# Revit family: BVR-R
name_source: partatom
category: Арматура трубопроводов
units: mm (PartAtom-declared; Revit-internal decimal feet)

## family parameters
Всегда вертикально = Да
На основе рабочей плоскости = Нет
Общий = Нет
При загрузке вырезать с полостями = Нет
Размер круглого соединителя = Использовать диаметр
Тип детали = Вставляется

## types (9) — shared parameters
ADSK_Версия Revit = 2019
ADSK_Версия семейства = 1.0
ADSK_Единица измерения = шт.
ADSK_Завод-изготовитель = ООО «Ридан-Трейд»
ADSK_Количество = 1
ADSK_Материал = Латунь Никелированная
ADSK_Потеря давления жидкости = 0.0 Па
ADSK_Расход жидкости = 0.0000 м³/ч
LT = BVR-R
URL = https://ridan.ru

## per-type parameters (varying)
| type | ADSK_Диаметр условный | ADSK_Код изделия | ADSK_Марка | ADSK_Масса | ADSK_Наименование | ADSK_Пропускная способность | a | b | c | d | e | f | g | h | i | j | k | l | m | n | o | p | УГО_Длина |
| DN15 | 15 мм | 065B8307RG | BVR-R DN15 | 0.23 | Кран шаровой ГОСТ BVR-R полнопроходной с внутренней резьбой PN40, Tmax=120C, DN15 | 15.0000 м³/ч | 18 мм | 4 мм | 2 мм | 10 мм | 1 мм | 11 мм | 15 мм | 7 мм | 29 мм | 24 мм | 31 мм | 25 мм | 19 мм | 16 мм | 29 мм | 29 мм | 29 мм |
| DN20 | 20 мм | 065B8308RG | BVR-R DN20 | 0.33 | Кран шаровой ГОСТ BVR-R полнопроходной с внутренней резьбой PN40, Tmax=120C, DN20 | 28.0000 м³/ч | 19 мм | 4 мм | 3 мм | 15 мм | 2 мм | 11 мм | 18 мм | 9 мм | 36 мм | 31 мм | 38 мм | 31 мм | 24 мм | 16 мм | 33 мм | 33 мм | 33 мм |
| DN25 | 25 мм | 065B8309RG | BVR-R DN25 | 0.55 | Кран шаровой ГОСТ BVR-R полнопроходной с внутренней резьбой PN40, Tmax=120C, DN25 | 39.0000 м³/ч | 23 мм | 5 мм | 3 мм | 17 мм | 1 мм | 12 мм | 22 мм | 11 мм | 45 мм | 38 мм | 47 мм | 38 мм | 30 мм | 19 мм | 40 мм | 39 мм | 39 мм |
| DN32 | 32 мм | 065B8310RG | BVR-R DN30 | 0.73 | Кран шаровой ГОСТ BVR-R полнопроходной с внутренней резьбой PN40, Tmax=120C, DN32 | 84.0000 м³/ч | 26 мм | 5 мм | 4 мм | 23 мм | 2 мм | 12 мм | 24 мм | 13 мм | 55 мм | 47 мм | 57 мм | 47 мм | 39 мм | 19 мм | 45 мм | 47 мм | 47 мм |
| DN40 | 40 мм | 065B8311RG | BVR-R DN35 | 1.2 | Кран шаровой ГОСТ BVR-R полнопроходной с внутренней резьбой PN40, Tmax=120C, DN40 | 156.0000 м³/ч | 26 мм | 4 мм | 6 мм | 29 мм | 1 мм | 15 мм | 26 мм | 18 мм | 66 мм | 55 мм | 68 мм | 54 мм | 45 мм | 22 мм | 52 мм | 55 мм | 55 мм |
| DN50 | 50 мм | 065B8312RG | BVR-R DN40 | 1.76 | Кран шаровой ГОСТ BVR-R полнопроходной с внутренней резьбой PN40, Tmax=120C, DN50 | 243.0000 м³/ч | 29 мм | 7 мм | 8 мм | 36 мм | 1 мм | 16 мм | 31 мм | 20 мм | 82 мм | 66 мм | 84 мм | 66 мм | 57 мм | 22 мм | 59 мм | 68 мм | 68 мм |
| DN65 | 65 мм | 065B8313RG | BVR-R DN45 | 3.38 | Кран шаровой ГОСТ BVR-R полнопроходной с внутренней резьбой PN25, Tmax=120C, DN65 | 476.0000 м³/ч | 27 мм | 8 мм | 10 мм | 43 мм | 2 мм | 17 мм | 26 мм | 21 мм | 101 мм | 81 мм | 104 мм | 84 мм | 72 мм | 38 мм | 81 мм | 80 мм | 80 мм |
| DN80 | 80 мм | 065B8314RG | BVR-R DN50 | 4.7 | Кран шаровой ГОСТ BVR-R полнопроходной с внутренней резьбой PN25, Tmax=120C, DN80 | 770.0000 м³/ч | 28 мм | 8 мм | 12 мм | 52 мм | 1 мм | 22 мм | 27 мм | 27 мм | 120 мм | 96 мм | 122 мм | 96 мм | 85 мм | 38 мм | 91 мм | 96 мм | 96 мм |
| DN100 | 100 мм | 065B8315RG | BVR-R DN55 | 8.54 | Кран шаровой ГОСТ BVR-R полнопроходной с внутренней резьбой PN25, Tmax=120C, DN100 | 1200.0000 м³/ч | 30 мм | 13 мм | 14 мм | 67 мм | 2 мм | 25 мм | 31 мм | 35 мм | 150 мм | 122 мм | 152 мм | 123 мм | 110 мм | 46 мм | 116 мм | 120 мм | 120 мм |
